# Revit family: SpecEquip_SAYFA_Ladder_Vista Maxi
name_source: partatom
category: Specialty Equipment
revit_build: Autodesk Revit 2015 (Build: 20140606_1530(x64)
units: mm (PartAtom-declared; Revit-internal decimal feet)

## types (8) — shared parameters
Description = Vista Ladder Maxi
Manufacturer = Sayfa
Manufacturer_Spec Code = LD463 Maxi
Manufacturer_URL__Product Specific = http://sayfa.com.au
Material_ANZRS = z_Sayfa_Metal_Steel
Model = LD463 Maxi
Type Comments = Ladder Maxi
URL = http://www.sayfa.com.au

## per-type parameters (varying)
| type | Ceiling to Roof Height (A) | Roof Hatch Type | Suspension Kit Clear Width (A2) |
| 1600mm Ceiling to Roof Height | 1600 mm  [stored 5.24934 ft] | SpecEquip_SAYFA_Roof Hatch : Roof Deck Mount | 2230 mm |
| 0400mm Ceiling to Roof Height | 400 mm  [stored 1.31234 ft] | SpecEquip_SAYFA_Roof Hatch : Roof Deck Mount | 1910 mm |
| 0800mm Ceiling to Roof Height | 800 mm  [stored 2.62467 ft] | SpecEquip_SAYFA_Roof Hatch : Roof Deck Mount | 2020 mm |
| 1200mm Ceiling to Roof Height | 1200 mm | SpecEquip_SAYFA_Roof Hatch : Concrete Mount | 2130 mm |
| 2000mm Ceiling to Roof Height | 2000 mm  [stored 6.56168 ft] | SpecEquip_SAYFA_Roof Hatch : Roof Deck Mount | 2340 mm |
| 2400mm Ceiling to Roof Height | 2400 mm | SpecEquip_SAYFA_Roof Hatch : Roof Deck Mount | 2450 mm  [stored 8.03806 ft] |
| 2800mm Ceiling to Roof Height | 2800 mm | SpecEquip_SAYFA_Roof Hatch : Roof Deck Mount | 2570 mm |
| 3000mm Ceiling to Roof Height | 3000 mm  [stored 9.84252 ft] | SpecEquip_SAYFA_Roof Hatch : Roof Deck Mount | 2600 mm  [stored 8.53018 ft] |

note: [stored X ft] marks values corroborated as IEEE doubles in the binary element streams (Revit-internal decimal feet)

## geometry (parser evidence)
native form markers: Sweep x22
no freeform markers — native parametric forms only
